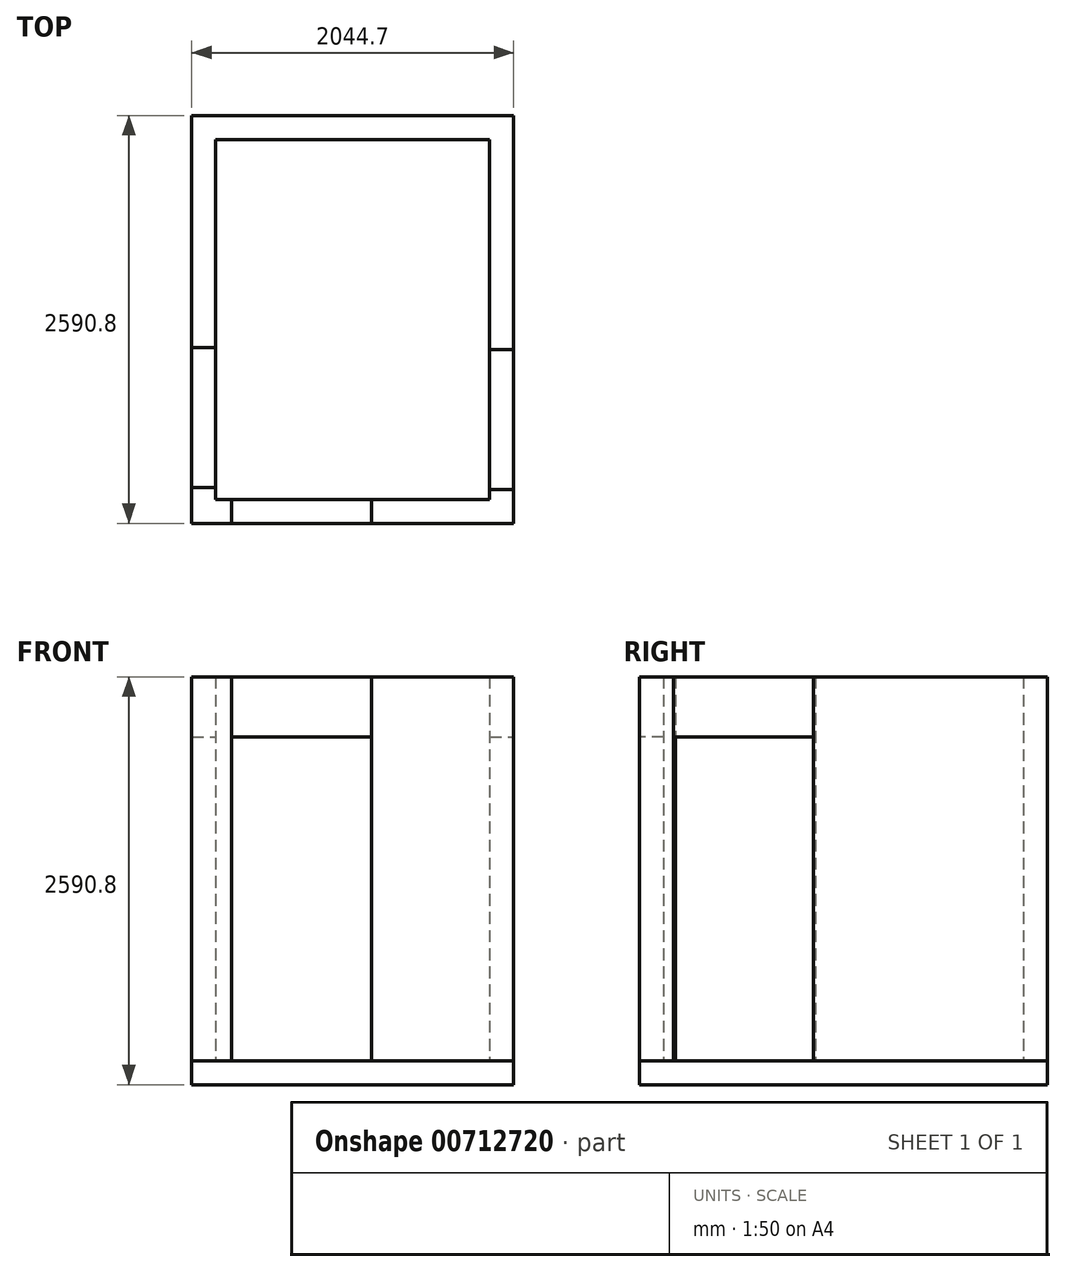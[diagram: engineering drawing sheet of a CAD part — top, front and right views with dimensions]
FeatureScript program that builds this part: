
annotation { "Feature Type Name" : "Feature", "Feature Type Description" : "" }
export const myFeature = defineFeature(function(context is Context, id is Id, definition is map)
    precondition{}
    {
        {
            var Q0;
            Q0=qCreatedBy(makeId("Top.planeOp"),FACE);
            var sketch = newSketch(context, id + "F0", { "sketchPlane" : qUnion([Q0])});
            skLineSegment(sketch, "E0.bottom", {"start": v(0, 0) * mm, "end": v(1739.9, 0) * mm});
            skLineSegment(sketch, "E0.top", {"start": v(0, 2286) * mm, "end": v(1739.9, 2286) * mm});
            skLineSegment(sketch, "E0.left", {"start": v(0, 0) * mm, "end": v(0, 2286) * mm});
            skLineSegment(sketch, "E0.right", {"start": v(1739.9, 0) * mm, "end": v(1739.9, 2286) * mm});
            skLineSegment(sketch, "E1.0", {"start": v(-152.4, 2438.4) * mm, "end": v(1892.3, 2438.4) * mm});
            skLineSegment(sketch, "E1.1", {"start": v(-152.4, -152.4) * mm, "end": v(-152.4, 2438.4) * mm});
            skLineSegment(sketch, "E1.2", {"start": v(-152.4, -152.4) * mm, "end": v(1892.3, -152.4) * mm});
            skLineSegment(sketch, "E1.3", {"start": v(1892.3, -152.4) * mm, "end": v(1892.3, 2438.4) * mm});
            skLineSegment(sketch, "E2", {"start": v(-152.4, 965.2) * mm, "end": v(0, 965.2) * mm});
            skLineSegment(sketch, "E3", {"start": v(-152.4, 76.2) * mm, "end": v(0, 76.2) * mm});
            skLineSegment(sketch, "E4", {"start": v(101.6, 0) * mm, "end": v(101.6, -152.4) * mm});
            skLineSegment(sketch, "E5", {"start": v(990.6, 0) * mm, "end": v(990.6, -152.4) * mm});
            skLineSegment(sketch, "E6", {"start": v(1739.9, 63.5) * mm, "end": v(1892.3, 63.5) * mm});
            skLineSegment(sketch, "E7", {"start": v(1739.9, 952.5) * mm, "end": v(1892.3, 952.5) * mm});
            skArc(sketch, "E8", {"start": v(850.9, 952.5) * mm, "mid": v(1111.28, 323.88) * mm, "end": v(1739.9, 63.5) * mm});
            skArc(sketch, "E9", {"start": v(990.6, 0) * mm, "mid": v(730.22, 628.62) * mm, "end": v(101.6, 889) * mm});
            skArc(sketch, "E10", {"start": v(889, 76.2) * mm, "mid": v(628.62, 704.82) * mm, "end": v(0, 965.2) * mm});
            skLineSegment(sketch, "E11", {"start": v(850.9, 952.5) * mm, "end": v(1739.9, 952.5) * mm});
            skLineSegment(sketch, "E12", {"start": v(101.6, 889) * mm, "end": v(101.6, 0) * mm});
            skLineSegment(sketch, "E13", {"start": v(0, 76.2) * mm, "end": v(889, 76.2) * mm});
            skSolve(sketch);
        }
        {
            var Q0;
            {var subQ2=sQuery(id+"F0.wireOp",EDGE,"E0.top");Q0=makeQuery(id+"F0.imprint","IMPRINT",FACE,{"disambiguationData":[TD([[makeQuery(id+"F0.imprint","IMPRINT",EDGE,{"derivedFrom":subQ2}),1.0]])]});}
            var Q1;
            {var subQ3=sQuery(id+"F0.wireOp",EDGE,"E5");Q1=makeQuery(id+"F0.imprint","IMPRINT",FACE,{"disambiguationData":[TD([[makeQuery(id+"F0.imprint","IMPRINT",EDGE,{"derivedFrom":subQ3}),1.0]])]});}
            var Q2;
            {var subQ3=sQuery(id+"F0.wireOp",EDGE,"E3");Q2=makeQuery(id+"F0.imprint","IMPRINT",FACE,{"disambiguationData":[TD([[makeQuery(id+"F0.imprint","IMPRINT",EDGE,{"derivedFrom":subQ3}),-1.0]])]});}
            extrude(context, id + "F1", {"entities" : qUnion([Q0, Q1, Q2]), "depth" : 2438.4 * mm, "offsetDistance" : 25.4 * mm});
        }
        {
            var Q0;
            {var subQ0=sQuery(id+"F0.wireOp",EDGE,"E2");Q0=makeQuery(id+"F0.imprint","IMPRINT",FACE,{"disambiguationData":[TD([[makeQuery(id+"F0.imprint","IMPRINT",EDGE,{"derivedFrom":subQ0}),-1.0]])]});}
            var Q1;
            {var subQ0=sQuery(id+"F0.wireOp",EDGE,"E6");Q1=makeQuery(id+"F0.imprint","IMPRINT",FACE,{"disambiguationData":[TD([[makeQuery(id+"F0.imprint","IMPRINT",EDGE,{"derivedFrom":subQ0}),1.0]])]});}
            var Q2;
            {var subQ0=sQuery(id+"F0.wireOp",EDGE,"E4");Q2=makeQuery(id+"F0.imprint","IMPRINT",FACE,{"disambiguationData":[TD([[makeQuery(id+"F0.imprint","IMPRINT",EDGE,{"derivedFrom":subQ0}),1.0]])]});}
            extrude(context, id + "F2", {"entities" : qUnion([Q0, Q1, Q2]), "depth" : 2438.4 * mm, "offsetDistance" : 25.4 * mm, "hasSecondDirection" : true, "secondDirectionOppositeDirection" : true, "secondDirectionDepth" : -2057.4 * mm});
        }
        {
            var Q0;
            Q0 = qSketchRegion(id + "F0", true);
            var Q1;
            {var subQ0=sQuery(id+"F0.wireOp",EDGE,"E8");Q1=makeQuery(id+"F0.imprint","IMPRINT",FACE,{"disambiguationData":[TD([[makeQuery(id+"F0.imprint","IMPRINT",EDGE,{"derivedFrom":subQ0}),1.0]])]});}
            var Q2;
            {var subQ1=sQuery(id+"F0.wireOp",EDGE,"E0.top");Q2=makeQuery(id+"F0.imprint","IMPRINT",FACE,{"disambiguationData":[TD([[makeQuery(id+"F0.imprint","IMPRINT",EDGE,{"derivedFrom":subQ1}),-1.0]])]});}
            var Q3;
            {var subQ0=sQuery(id+"F0.wireOp",EDGE,"E12");var subQ1=sQuery(id+"F0.wireOp",EDGE,"E9");var subQ2=makeQuery(id+"F0.imprint","INTERSECT",VERTEX,{"derivedFrom":[subQ1,subQ0]});Q3=makeQuery(id+"F0.imprint","IMPRINT",FACE,{"disambiguationData":[TD([[makeQuery(id+"F0.imprint","IMPRINT",EDGE,{"disambiguationData":[TD([[subQ2,1.0]])],"derivedFrom":subQ1}),1.0]])]});}
            var Q4;
            {var subQ0=sQuery(id+"F0.wireOp",EDGE,"E12");var subQ1=sQuery(id+"F0.wireOp",EDGE,"E9");var subQ2=makeQuery(id+"F0.imprint","INTERSECT",VERTEX,{"derivedFrom":[subQ1,subQ0]});Q4=makeQuery(id+"F0.imprint","IMPRINT",FACE,{"disambiguationData":[TD([[makeQuery(id+"F0.imprint","IMPRINT",EDGE,{"disambiguationData":[TD([[subQ2,1.0]])],"derivedFrom":subQ1}),-1.0]])]});}
            var Q5;
            {var subQ3=sQuery(id+"F0.wireOp",EDGE,"E13");var subQ5=sQuery(id+"F0.wireOp",EDGE,"E10");var subQ6=makeQuery(id+"F0.imprint","INTERSECT",VERTEX,{"derivedFrom":[subQ5,subQ3]});Q5=makeQuery(id+"F0.imprint","IMPRINT",FACE,{"disambiguationData":[TD([[makeQuery(id+"F0.imprint","IMPRINT",EDGE,{"disambiguationData":[TD([[subQ6,-1.0]])],"derivedFrom":subQ5}),-1.0]])]});}
            var Q6;
            {var subQ0=sQuery(id+"F0.wireOp",EDGE,"E0.left");var subQ1=sQuery(id+"F0.wireOp",EDGE,"E0.bottom");var subQ2=makeQuery(id+"F0.imprint","INTERSECT",VERTEX,{"derivedFrom":[subQ1,subQ0]});Q6=makeQuery(id+"F0.imprint","IMPRINT",FACE,{"disambiguationData":[TD([[makeQuery(id+"F0.imprint","IMPRINT",EDGE,{"disambiguationData":[TD([[subQ2,-1.0]])],"derivedFrom":subQ1}),1.0]])]});}
            extrude(context, id + "F3", {"entities" : qUnion([Q0, Q1, Q2, Q3, Q4, Q5, Q6]), "oppositeDirection" : true, "depth" : 152.4 * mm, "offsetDistance" : 25.4 * mm});
        }
    });
